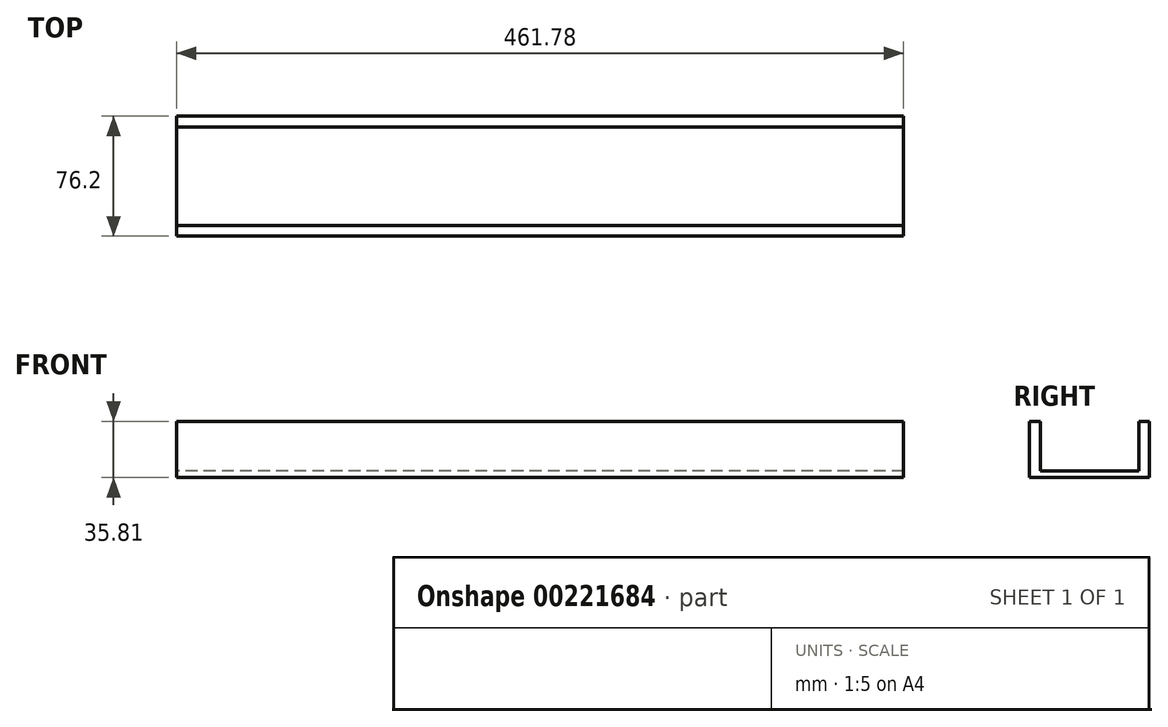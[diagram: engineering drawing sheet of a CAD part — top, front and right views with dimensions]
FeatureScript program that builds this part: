
annotation { "Feature Type Name" : "Feature", "Feature Type Description" : "" }
export const myFeature = defineFeature(function(context is Context, id is Id, definition is map)
    precondition{}
    {
        {
            var Q0;
            Q0=qCreatedBy(makeId("Top.planeOp"),FACE);
            var sketch = newSketch(context, id + "F0", { "sketchPlane" : qUnion([Q0])});
            skLineSegment(sketch, "E0.bottom", {"start": v(-269.58, 47.3) * mm, "end": v(192.2, 47.3) * mm});
            skLineSegment(sketch, "E0.top", {"start": v(-269.58, -28.9) * mm, "end": v(192.2, -28.9) * mm});
            skLineSegment(sketch, "E0.left", {"start": v(-269.58, 47.3) * mm, "end": v(-269.58, -28.9) * mm});
            skLineSegment(sketch, "E0.right", {"start": v(192.2, 47.3) * mm, "end": v(192.2, -28.9) * mm});
            skSolve(sketch);
        }
        {
            var Q0;
            Q0 = qSketchRegion(id + "F0", true);
            extrude(context, id + "F1", {"entities" : qUnion([Q0]), "depth" : 35.81 * mm});
        }
        {
            var Q0;
            Q0=makeQuery(id+"F1.opExtrude","SWEPT_FACE",FACE,{"disambiguationData":[OSD([sQuery(id+"F0.wireOp",EDGE,"E0.left")])]});
            var sketch = newSketch(context, id + "F2", { "sketchPlane" : qUnion([Q0])});
            skLineSegment(sketch, "E1.bottom", {"start": v(-40.37, 35.81) * mm, "end": v(21.96, 35.81) * mm});
            skLineSegment(sketch, "E1.top", {"start": v(-40.37, 4.32) * mm, "end": v(21.96, 4.32) * mm});
            skLineSegment(sketch, "E1.left", {"start": v(-40.37, 35.81) * mm, "end": v(-40.37, 4.32) * mm});
            skLineSegment(sketch, "E1.right", {"start": v(21.96, 35.81) * mm, "end": v(21.96, 4.32) * mm});
            skSolve(sketch);
        }
        {
            var Q0;
            Q0 = qSketchRegion(id + "F2", true);
            extrude(context, id + "F3", {"entities" : qUnion([Q0]), "operationType" : NewBodyOperationType.REMOVE, "endBound" : BoundingType.THROUGH_ALL, "oppositeDirection" : true, "depth" : 25.4 * mm});
        }
    });
